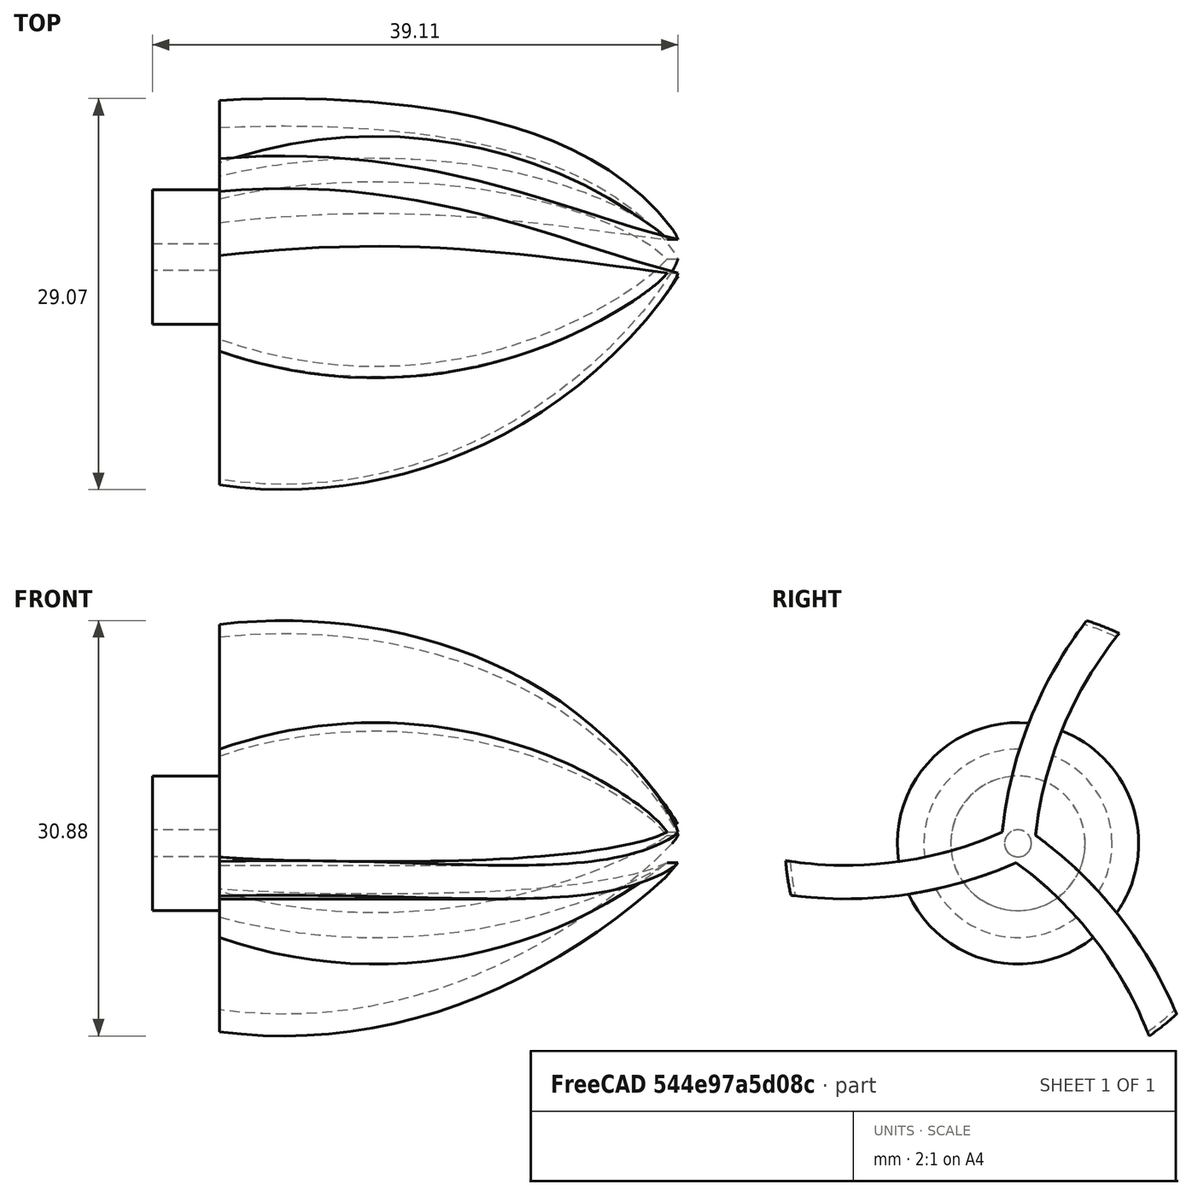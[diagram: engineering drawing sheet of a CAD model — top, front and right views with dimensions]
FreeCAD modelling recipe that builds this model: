
FCSTD DOCUMENT  (FreeCAD 0.18R4 (GitTag))
Label: Ariel Propeller Right
License: All rights reserved
LicenseURL: http://en.wikipedia.org/wiki/All_rights_reserved
objects: Sketcher::SketchObject×5, PartDesign::Revolution×1, PartDesign::AdditivePipe×1, PartDesign::PolarPattern×1, PartDesign::Groove×1, Part::Plane×1, PartDesign::Pad×1, PartDesign::Body×1, Mesh::Feature×1
note: 16 computed .brp shape members not serialized (recipe doc carries the construction recipe); baked Part::Feature solids carry a one-line shape summary decoded from their .brp

FEATURE [Sketcher::SketchObject] Sketch
  MapMode = 5
  Support = -> [XY_Plane]
  sketch-geometry (3):
    g0: LineSegment StartX=10 StartY=7 StartZ=0 EndX=10 EndY=0 EndZ=0
    g1: ArcOfCircle CenterX=21.5953 CenterY=-26.0235 CenterZ=0 NormalX=0 NormalY=0 NormalZ=1 AngleXU=0 Radius=35 StartAngle=0.83833 EndAngle=1.90847
    g2: LineSegment StartX=10 StartY=0 StartZ=0 EndX=45 EndY=-7.6525e-12 EndZ=0
  constraints (10):
    c: Vertical(g0)
    c: PointOnObject(g0,g-1)
    c: PointOnObject(g1,g-1)
    c: Radius(g1) = 35
    c: Coincident(g2,g0)
    c: Coincident(g2,g1)
    c: DistanceX(g-1,g0) = 10
    c: DistanceX(g-1,g1) = 45
    c: Coincident(g1,g0)
    c: DistanceY(g0,g0) = 7
FEATURE [PartDesign::Revolution] Revolution
  Angle = 360
  Axis = (1,0,0)
  Base = (0,0,0)
  Profile = -> Sketch
  ReferenceAxis = -> Sketch [H_Axis]
FEATURE [Sketcher::SketchObject] Sketch002
  MapMode = 5
  Support = -> [XY_Plane]
  sketch-geometry (6):
    g0: ArcOfCircle [constr] CenterX=21.5953 CenterY=26.0235 CenterZ=0 NormalX=0 NormalY=0 NormalZ=1 AngleXU=0 Radius=35 StartAngle=4.37471 EndAngle=5.44486
    g1: LineSegment [constr] StartX=10 StartY=7 StartZ=0 EndX=10 EndY=-7 EndZ=0
    g2: LineSegment StartX=10 StartY=1.25 StartZ=0 EndX=10 EndY=-1.25 EndZ=0
    g3: LineSegment StartX=10 StartY=1.25 StartZ=0 EndX=45 EndY=1.25 EndZ=0
    g4: LineSegment StartX=10 StartY=-1.25 StartZ=0 EndX=45 EndY=-1.25 EndZ=0
    g5: LineSegment StartX=45 StartY=1.25 StartZ=0 EndX=45 EndY=-1.25 EndZ=0
  constraints (13):
    c: Coincident(g1,g0)
    c: DistanceY(g1,g1) = 14
    c: PointOnObject(g2,g1)
    c: Symmetric(g2,g2,g-1)
    c: DistanceY(g2,g2) = 2.5
    c: Coincident(g3,g2)
    c: Coincident(g4,g2)
    c: Coincident(g5,g3)
    c: Coincident(g5,g4)
    c: DistanceY(g5,g5) = 2.5
    c: Horizontal(g3)
    c: PointOnObject(g0,g5)
    c: Vertical(g3,g4)
FEATURE [Sketcher::SketchObject] Sketch003
  ExternalGeometry = -> [Sketch002]
  MapMode = 5
  Placement = pos=(0,0,0) rot=(0.57735,0.57735,0.57735;2.0944rad)
  Support = -> [YZ_Plane]
  sketch-geometry (1):
    g0: ArcOfCircle CenterX=29.8998 CenterY=-2.4499 CenterZ=0 NormalX=0 NormalY=0 NormalZ=1 AngleXU=0 Radius=30 StartAngle=2.29605 EndAngle=3.05984
  constraints (4):
    c: Coincident(g0,g-1)
    c: DistanceX(g-1,g0) = 10
    c: DistanceY(g-1,g0) = 20
    c: Radius(g0) = 30
FEATURE [PartDesign::AdditivePipe] AdditivePipe
  AuxilleryCurvelinear = true
  AuxillerySpineTangent = false
  BaseFeature = -> Revolution
  Binormal = (0,0,0)
  Mode = 0
  Profile = -> Sketch002
  Spine = -> Sketch003
  SpineTangent = false
  Transformation = 0
  Transition = 0
FEATURE [PartDesign::PolarPattern] PolarPattern
  Angle = 360
  Axis = -> X_Axis
  BaseFeature = -> AdditivePipe
  Occurrences = 3
  Originals = -> [AdditivePipe]
FEATURE [Sketcher::SketchObject] Sketch004
  ExternalGeometry = -> [PolarPattern]
  MapMode = 5
  Support = -> [XY_Plane]
  sketch-geometry (3):
    g0: ArcOfCircle CenterX=14.7884 CenterY=-17.6709 CenterZ=0 NormalX=0 NormalY=0 NormalZ=1 AngleXU=0 Radius=35 StartAngle=0.529246 EndAngle=1.70804
    g1: ArcOfCircle CenterX=10.9237 CenterY=-7.98781 CenterZ=0 NormalX=0 NormalY=0 NormalZ=1 AngleXU=0 Radius=35 StartAngle=0.230252 EndAngle=1.59719
    g2: LineSegment StartX=10 StartY=27 StartZ=0 EndX=10 EndY=17 EndZ=0
FEATURE [PartDesign::Groove] Groove
  Angle = 360
  Axis = (1,0,0)
  Base = (0,0,0)
  BaseFeature = -> PolarPattern
  Profile = -> Sketch004
  ReferenceAxis = -> X_Axis
FEATURE [Part::Plane] Plane
  AttacherType = Attacher::AttachEngine3D
  Length = 10
  Placement = pos=(5,0,0) rot=(0.57735,0.57735,0.57735;2.0944rad)
  Width = 10
FEATURE [Sketcher::SketchObject] Sketch001
  MapMode = 5
  Placement = pos=(5,0,0) rot=(0.57735,0.57735,0.57735;2.0944rad)
  Support = -> [Plane]
  sketch-geometry (2):
    g0: Circle CenterX=0 CenterY=0 CenterZ=0 NormalX=0 NormalY=0 NormalZ=1 AngleXU=0 Radius=5
    g1: Circle CenterX=0 CenterY=0 CenterZ=0 NormalX=0 NormalY=0 NormalZ=1 AngleXU=0 Radius=1
  constraints (4):
    c: Radius(g0) = 5
    c: Coincident(g1,g0)
    c: Radius(g1) = 1
    c: Coincident(g0,g-1)
FEATURE [PartDesign::Pad] Pad
  BaseFeature = -> Groove
  Length = 10
  Length2 = 100
  Profile = -> Sketch001
  Type = 0
FEATURE [PartDesign::Body] Body
  Group = -> [Sketch,Revolution,Sketch001,Sketch002,Sketch003,AdditivePipe,PolarPattern,Sketch004,Groove,Pad]
  Origin = -> Origin
  Tip = -> Pad
FEATURE [Mesh::Feature] Mesh  label="Body (Meshed)"
